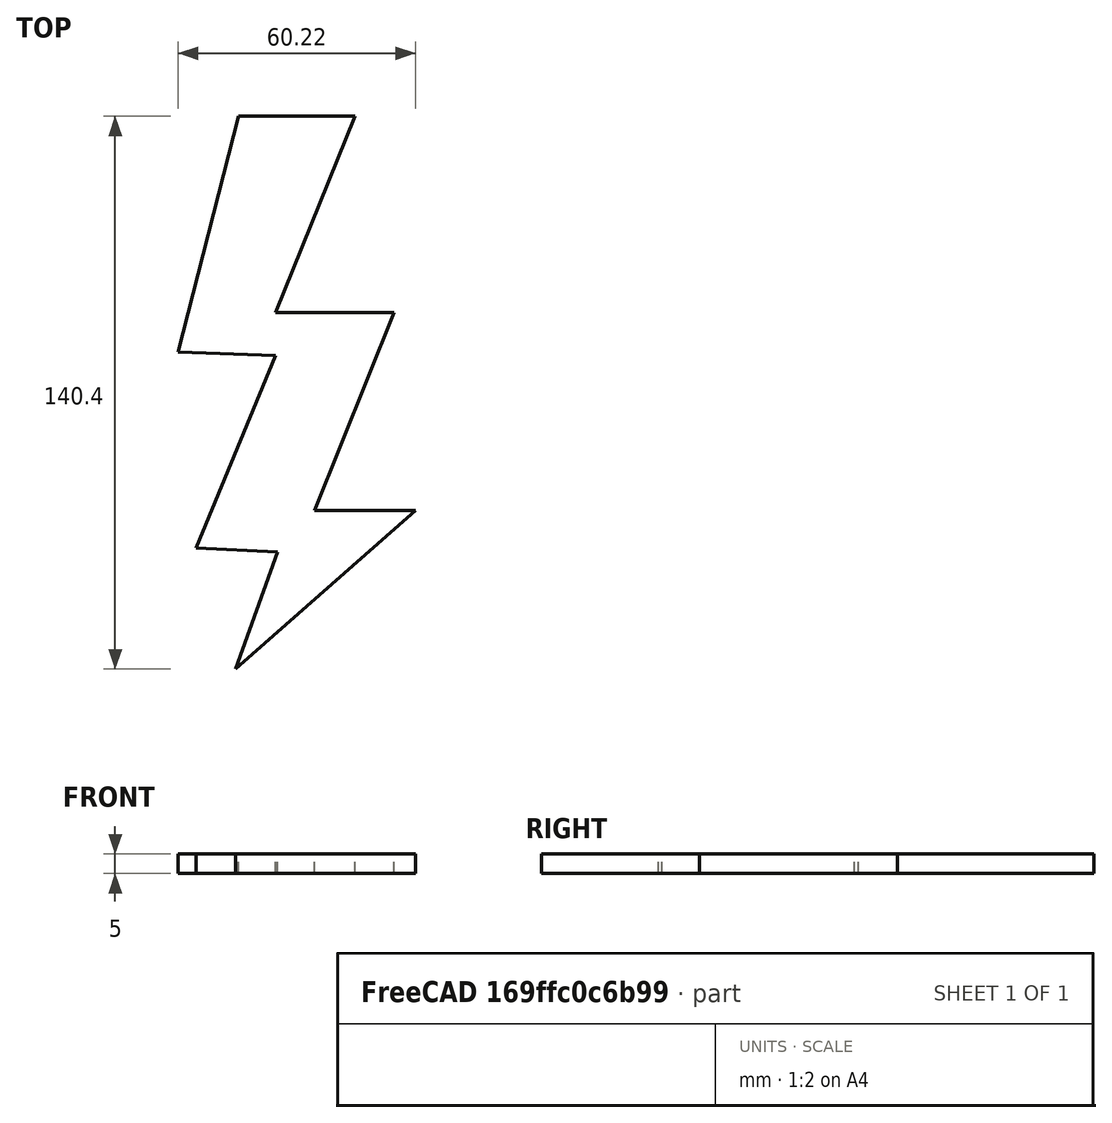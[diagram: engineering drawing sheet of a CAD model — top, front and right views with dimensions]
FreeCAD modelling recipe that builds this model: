
FCSTD DOCUMENT  (FreeCAD 0.21R33694 (Git))
Label: OJT1_T016R03_llamp
License: All rights reserved
LicenseURL: http://en.wikipedia.org/wiki/All_rights_reserved
objects: Sketcher::SketchObject×1, PartDesign::Pad×1, PartDesign::Body×1
note: 4 computed .brp shape members not serialized (recipe doc carries the construction recipe); baked Part::Feature solids carry a one-line shape summary decoded from their .brp

FEATURE [Sketcher::SketchObject] Sketch
  FullyConstrained = false
  MapMode = 5
  Support = -> [XY_Plane]
  sketch-geometry (11):
    g0: LineSegment StartX=19.9369 StartY=69.7204 StartZ=0 EndX=49.6185 EndY=69.7204 EndZ=0
    g1: LineSegment StartX=49.6185 StartY=69.7204 StartZ=0 EndX=29.4185 EndY=19.8389 EndZ=0
    g2: LineSegment StartX=29.4185 StartY=19.8389 StartZ=0 EndX=59.5123 EndY=19.8389 EndZ=0
    g3: LineSegment StartX=59.5123 StartY=19.8389 StartZ=0 EndX=39.3123 EndY=-30.4549 EndZ=0
    g4: LineSegment StartX=39.3123 StartY=-30.4549 StartZ=0 EndX=64.8715 EndY=-30.4549 EndZ=0
    g5: LineSegment StartX=64.8715 StartY=-30.4549 StartZ=0 EndX=19.2471 EndY=-70.6763 EndZ=0
    g6: LineSegment StartX=19.2471 StartY=-70.6763 StartZ=0 EndX=29.8209 EndY=-40.9689 EndZ=0
    g7: LineSegment StartX=29.8209 StartY=-40.9689 StartZ=0 EndX=9.17673 EndY=-39.9618 EndZ=0
    g8: LineSegment StartX=9.17673 StartY=-39.9618 StartZ=0 EndX=29.3174 EndY=8.87921 EndZ=0
    g9: LineSegment StartX=29.3174 StartY=8.87921 StartZ=0 EndX=4.64508 EndY=9.88625 EndZ=0
    g10: LineSegment StartX=4.64508 StartY=9.88625 StartZ=0 EndX=19.9369 EndY=69.7204 EndZ=0
  constraints (14):
    c: Horizontal(g0)
    c: Coincident(g0,g1)
    c: Coincident(g1,g2)
    c: Horizontal(g2)
    c: Coincident(g2,g3)
    c: Coincident(g3,g4)
    c: Horizontal(g4)
    c: Coincident(g4,g5)
    c: Coincident(g5,g6)
    c: Coincident(g6,g7)
    c: Coincident(g7,g8)
    c: Coincident(g8,g9)
    c: Coincident(g9,g10)
    c: Coincident(g10,g0)
FEATURE [PartDesign::Pad] Pad
  Direction = (0,0,1)
  Length = 5
  Length2 = 10
  Profile = -> Sketch
  ReferenceAxis = -> Sketch [N_Axis]
  Type = 0
FEATURE [PartDesign::Body] Body
  Group = -> [Sketch,Pad]
  Origin = -> Origin
  Tip = -> Pad
